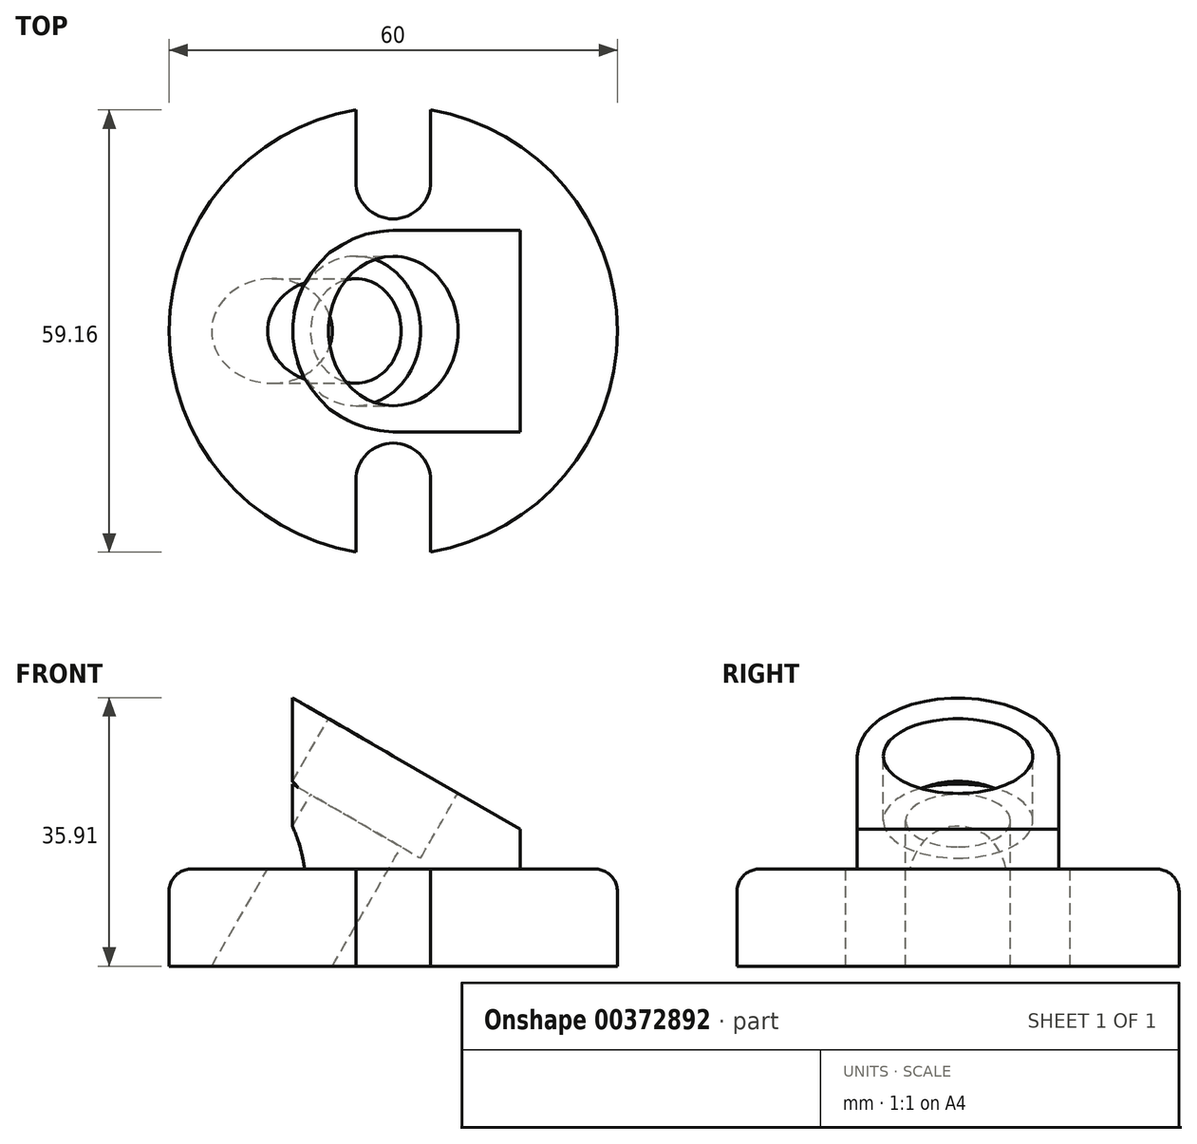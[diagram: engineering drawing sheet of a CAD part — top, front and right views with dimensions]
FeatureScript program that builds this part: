
annotation { "Feature Type Name" : "Feature", "Feature Type Description" : "" }
export const myFeature = defineFeature(function(context is Context, id is Id, definition is map)
    precondition{}
    {
        {
            var Q0;
            Q0=qCreatedBy(makeId("Top.planeOp"),FACE);
            var sketch = newSketch(context, id + "F0", { "sketchPlane" : qUnion([Q0])});
            skCircle(sketch, "E0", {"center": v(0, 0) * mm, "radius": 30 * mm});
            skSolve(sketch);
        }
        {
            var Q0;
            Q0 = qSketchRegion(id + "F0", true);
            extrude(context, id + "F1", {"entities" : qUnion([Q0]), "depth" : 13 * mm});
        }
        {
            var Q0;
            Q0=makeQuery(id+"F1.opExtrude","CAP_FACE",FACE,{"disambiguationData":[OSD([sQuery(id+"F0.wireOp",EDGE,"E0")])],"isStart":false});
            var sketch = newSketch(context, id + "F2", { "sketchPlane" : qUnion([Q0])});
            skPoint(sketch, "E1", {"position": v(0, -20) * mm});
            skCircle(sketch, "E2", {"center": v(0, -20) * mm, "radius": 5 * mm});
            skLineSegment(sketch, "E3", {"start": v(-5, -20) * mm, "end": v(-5, -29.58) * mm});
            skLineSegment(sketch, "E4", {"start": v(5, -20) * mm, "end": v(5, -29.58) * mm});
            skSolve(sketch);
        }
        {
            var Q0;
            {var subQ0=sQuery(id+"F2.wireOp",EDGE,"E3");Q0=makeQuery(id+"F2.imprint","IMPRINT",FACE,{"disambiguationData":[TD([[makeQuery(id+"F2.imprint","IMPRINT",EDGE,{"derivedFrom":subQ0}),1.0]])]});}
            var Q1;
            {var subQ0=sQuery(id+"F2.wireOp",EDGE,"E2");var subQ1=makeQuery(id+"F2.imprint","INTERSECT",VERTEX,{"derivedFrom":[subQ0,sQuery(id+"F2.wireOp",EDGE,"E3")]});Q1=makeQuery(id+"F2.imprint","IMPRINT",FACE,{"disambiguationData":[TD([[makeQuery(id+"F2.imprint","IMPRINT",EDGE,{"disambiguationData":[TD([[subQ1,1.0]])],"derivedFrom":subQ0}),1.0]])]});}
            extrude(context, id + "F3", {"entities" : qUnion([Q0, Q1]), "operationType" : NewBodyOperationType.REMOVE, "oppositeDirection" : true, "depth" : 25 * mm});
        }
        {
            var Q0;
            Q0=makeQuery(id+"F1.opExtrude","CAP_FACE",FACE,{"disambiguationData":[OSD([sQuery(id+"F0.wireOp",EDGE,"E0")])],"isStart":false});
            var sketch = newSketch(context, id + "F4", { "sketchPlane" : qUnion([Q0])});
            skPoint(sketch, "E5", {"position": v(0, 20) * mm});
            skCircle(sketch, "E6", {"center": v(0, 20) * mm, "radius": 5 * mm});
            skLineSegment(sketch, "E7", {"start": v(5, 20) * mm, "end": v(5, 29.58) * mm});
            skLineSegment(sketch, "E8", {"start": v(-5, 20) * mm, "end": v(-5, 29.58) * mm});
            skSolve(sketch);
        }
        {
            var Q0;
            Q0 = qSketchRegion(id + "F4", true);
            var Q1;
            {var subQ0=sQuery(id+"F4.wireOp",EDGE,"E7");Q1=makeQuery(id+"F4.imprint","IMPRINT",FACE,{"disambiguationData":[TD([[makeQuery(id+"F4.imprint","IMPRINT",EDGE,{"derivedFrom":subQ0}),1.0]])]});}
            extrude(context, id + "F5", {"entities" : qUnion([Q0, Q1]), "operationType" : NewBodyOperationType.REMOVE, "oppositeDirection" : true, "depth" : 25 * mm});
        }
        {
            var Q0;
            Q0=makeQuery(id+"F1.opExtrude","CAP_FACE",FACE,{"disambiguationData":[OSD([sQuery(id+"F0.wireOp",EDGE,"E0")])],"isStart":false});
            var sketch = newSketch(context, id + "F6", { "sketchPlane" : qUnion([Q0])});
            skCircle(sketch, "E9", {"center": v(0, 0) * mm, "radius": 13.5 * mm});
            skLineSegment(sketch, "E10", {"start": v(0, 13.5) * mm, "end": v(17, 13.5) * mm});
            skLineSegment(sketch, "E11", {"start": v(0, -13.5) * mm, "end": v(17, -13.5) * mm});
            skLineSegment(sketch, "E12", {"start": v(17, -13.5) * mm, "end": v(17, 13.5) * mm});
            skSolve(sketch);
        }
        {
            var Q0;
            Q0 = qSketchRegion(id + "F6", true);
            extrude(context, id + "F7", {"entities" : qUnion([Q0]), "operationType" : NewBodyOperationType.ADD, "depth" : 25 * mm});
        }
        {
            var Q0;
            Q0=qCreatedBy(makeId("Front.planeOp"),FACE);
            var sketch = newSketch(context, id + "F8", { "sketchPlane" : qUnion([Q0])});
            skLineSegment(sketch, "E13", {"start": v(-15, 18.3) * mm, "end": v(17, 18.3) * mm});
            skLineSegment(sketch, "E14", {"start": v(17, 18.3) * mm, "end": v(-14.92, 36.73) * mm});
            skLineSegment(sketch, "E15", {"start": v(-14.92, 36.73) * mm, "end": v(-15, 18.3) * mm});
            skLineSegment(sketch, "E16", {"start": v(17, 18.3) * mm, "end": v(17, 39.23) * mm});
            skLineSegment(sketch, "E17", {"start": v(17, 39.23) * mm, "end": v(-14.92, 39.23) * mm});
            skLineSegment(sketch, "E18", {"start": v(-14.92, 39.23) * mm, "end": v(-14.92, 36.73) * mm});
            skSolve(sketch);
        }
        {
            var Q0;
            Q0=makeQuery(id+"F8.imprint","IMPRINT",FACE,{"disambiguationData":[TD([[makeQuery(id+"F8.imprint","IMPRINT",EDGE,{"derivedFrom":sQuery(id+"F8.wireOp",EDGE,"E14")}),-1.0]])]});
            extrude(context, id + "F9", {"entities" : qUnion([Q0]), "operationType" : NewBodyOperationType.REMOVE, "endBound" : BoundingType.SYMMETRIC, "oppositeDirection" : true, "depth" : 50 * mm});
        }
        {
            var Q0;
            Q0=makeQuery(id+"F9.boolean.opBoolean","COPY",FACE,{"derivedFrom":makeQuery(id+"F9.opExtrude","SWEPT_FACE",FACE,{"disambiguationData":[OSD([sQuery(id+"F8.wireOp",EDGE,"E14")])]})});
            var sketch = newSketch(context, id + "F10", { "sketchPlane" : qUnion([Q0])});
            skCircle(sketch, "E19", {"center": v(-14.06, 0) * mm, "radius": 10 * mm});
            skCircle(sketch, "E20.0", {"center": v(-14.06, 0) * mm, "radius": 7 * mm});
            skSolve(sketch);
        }
        {
            var Q0;
            Q0 = qSketchRegion(id + "F10", true);
            extrude(context, id + "F11", {"entities" : qUnion([Q0]), "operationType" : NewBodyOperationType.REMOVE, "oppositeDirection" : true, "depth" : 10 * mm});
        }
        {
            var Q0;
            Q0=makeQuery(id+"F11.boolean.opBoolean","SPLIT",FACE,{"disambiguationData":[TD([makeQuery(id+"F11.opExtrude","SWEPT_FACE",FACE,{"disambiguationData":[OSD([sQuery(id+"F10.wireOp",EDGE,"E20.0")])]})])],"derivedFrom":makeQuery(id+"F9.boolean.opBoolean","COPY",FACE,{"derivedFrom":makeQuery(id+"F9.opExtrude","SWEPT_FACE",FACE,{"disambiguationData":[OSD([sQuery(id+"F8.wireOp",EDGE,"E14")])]})})});
            extrude(context, id + "F12", {"entities" : qUnion([Q0]), "operationType" : NewBodyOperationType.REMOVE, "endBound" : BoundingType.THROUGH_ALL, "oppositeDirection" : true, "depth" : 25 * mm});
        }
        {
            var Q0;
            {var subQ0=sQuery(id+"F0.wireOp",EDGE,"E0");Q0=makeQuery(id+"F5.boolean.opBoolean","SPLIT",EDGE,{"disambiguationData":[TD([makeQuery(id+"F3.boolean.opBoolean","COPY",FACE,{"derivedFrom":makeQuery(id+"F3.opExtrude","SWEPT_FACE",FACE,{"disambiguationData":[OSD([sQuery(id+"F2.wireOp",EDGE,"E3")])]})})])],"derivedFrom":makeQuery(id+"F1.opExtrude","CAP_EDGE",EDGE,{"disambiguationData":[OSD([subQ0])],"isStart":false})});}
            fillet(context, id + "F13", {"entities" : qUnion([Q0]), "radius" : 3 * mm, "tangentPropagation" : true, "allowEdgeOverflow" : false});
        }
        {
            var Q0;
            {var subQ0=sQuery(id+"F0.wireOp",EDGE,"E0");Q0=makeQuery(id+"F5.boolean.opBoolean","SPLIT",EDGE,{"disambiguationData":[TD([makeQuery(id+"F3.boolean.opBoolean","COPY",FACE,{"derivedFrom":makeQuery(id+"F3.opExtrude","SWEPT_FACE",FACE,{"disambiguationData":[OSD([sQuery(id+"F2.wireOp",EDGE,"E4")])]})})])],"derivedFrom":makeQuery(id+"F1.opExtrude","CAP_EDGE",EDGE,{"disambiguationData":[OSD([subQ0])],"isStart":false})});}
            fillet(context, id + "F14", {"entities" : qUnion([Q0]), "radius" : 3 * mm, "tangentPropagation" : true, "allowEdgeOverflow" : false});
        }
    });
